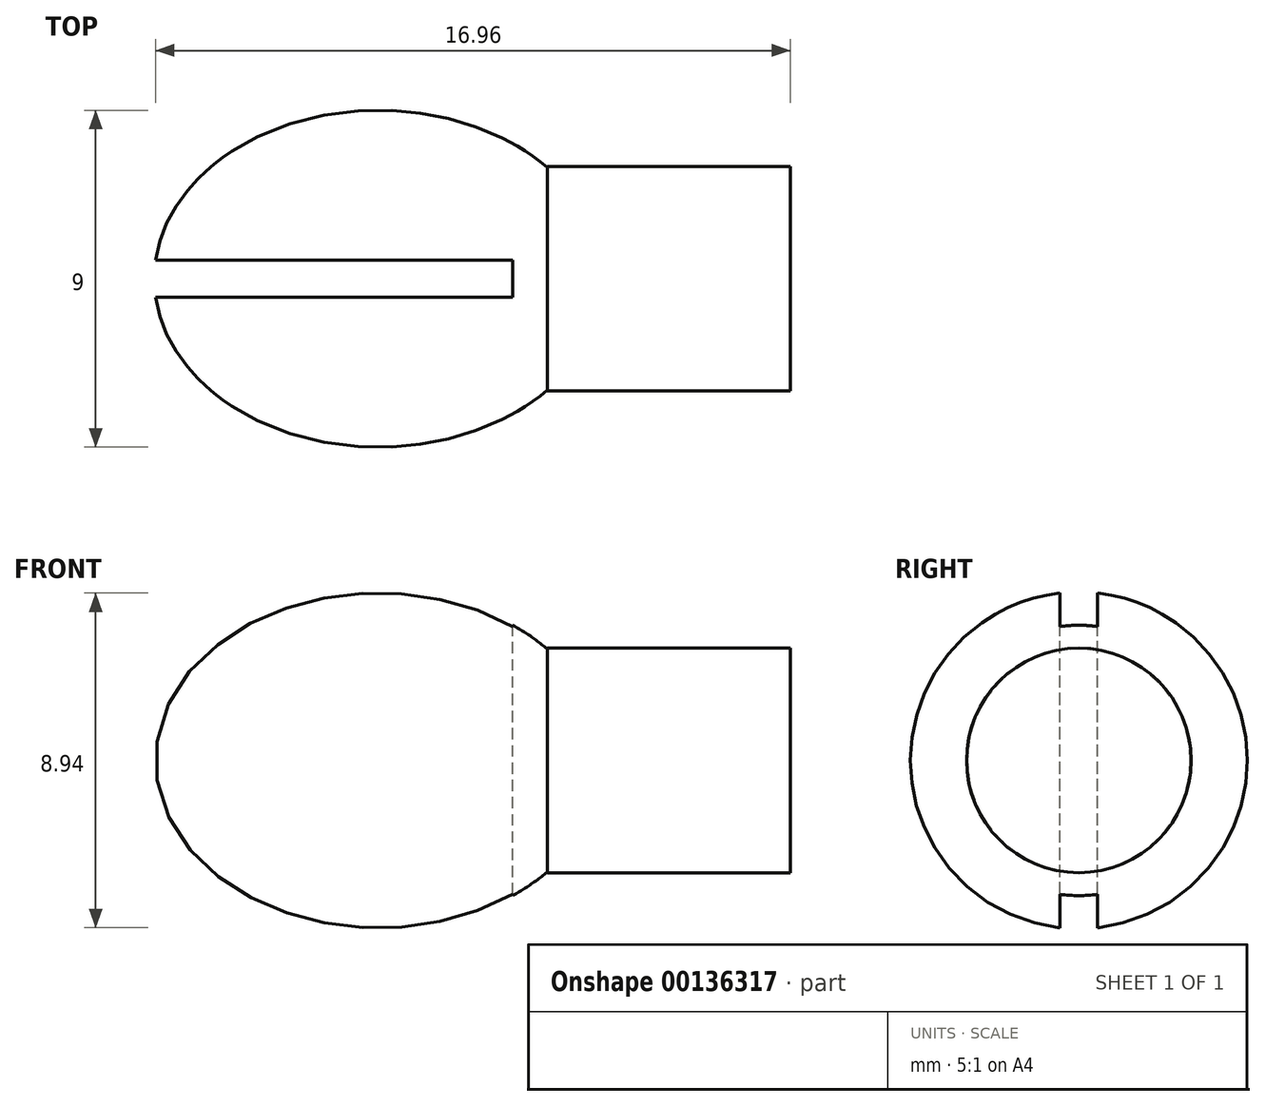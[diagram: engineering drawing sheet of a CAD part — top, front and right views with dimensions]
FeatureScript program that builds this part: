
annotation { "Feature Type Name" : "Feature", "Feature Type Description" : "" }
export const myFeature = defineFeature(function(context is Context, id is Id, definition is map)
    precondition{}
    {
        {
            var Q0;
            Q0=qCreatedBy(makeId("Front.planeOp"),FACE);
            var sketch = newSketch(context, id + "F0", { "sketchPlane" : qUnion([Q0])});
            skEllipse(sketch, "E0", {"center": v(0, 0) * mm, "majorRadius": 6 * mm, "minorRadius": 4.5 * mm, "majorAxis": v(1, 0)});
            skLineSegment(sketch, "E1", {"start": v(-6, 0) * mm, "end": v(6, 0) * mm});
            skSolve(sketch);
        }
        {
            var Q0;
            {var subQ0=sQuery(id+"F0.wireOp",EDGE,"E1");Q0=makeQuery(id+"F0.imprint","IMPRINT",FACE,{"disambiguationData":[TD([[makeQuery(id+"F0.imprint","IMPRINT",EDGE,{"derivedFrom":subQ0}),1.0]])]});}
            var Q1;
            Q1=sQuery(id+"F0.wireOp",EDGE,"E1");
            revolve(context, id + "F1", {"entities" : qUnion([Q0]), "axis" : qUnion([Q1]), "revolveType" : RevolveType.FULL});
        }
        {
            var Q0;
            Q0=qCreatedBy(makeId("Front.planeOp"),FACE);
            var sketch = newSketch(context, id + "F2", { "sketchPlane" : qUnion([Q0])});
            skLineSegment(sketch, "E2", {"start": v(4.5, 3) * mm, "end": v(4.5, -3) * mm});
            skLineSegment(sketch, "E3", {"start": v(4.5, 3) * mm, "end": v(4.5, 3.6) * mm});
            skLineSegment(sketch, "E4", {"start": v(4.5, 3.6) * mm, "end": v(6.38, 3.6) * mm});
            skLineSegment(sketch, "E5", {"start": v(6.38, 3.6) * mm, "end": v(6.38, -3.79) * mm});
            skLineSegment(sketch, "E6", {"start": v(6.38, -3.79) * mm, "end": v(4.5, -3.79) * mm});
            skLineSegment(sketch, "E7", {"start": v(4.5, -3.79) * mm, "end": v(4.5, -3) * mm});
            skSolve(sketch);
        }
        {
            var Q0;
            Q0=makeQuery(id+"F2.imprint","IMPRINT",FACE,{"disambiguationData":[TD([[makeQuery(id+"F2.imprint","IMPRINT",EDGE,{"derivedFrom":sQuery(id+"F2.wireOp",EDGE,"E2")}),1.0]])]});
            extrude(context, id + "F3", {"entities" : qUnion([Q0]), "operationType" : NewBodyOperationType.REMOVE, "endBound" : BoundingType.SYMMETRIC, "oppositeDirection" : true, "depth" : 25 * mm});
        }
        {
            var Q0;
            Q0=makeQuery(id+"F3.boolean.opBoolean","COPY",FACE,{"derivedFrom":makeQuery(id+"F3.opExtrude","SWEPT_FACE",FACE,{"disambiguationData":[OSD([sQuery(id+"F2.wireOp",EDGE,"E2"),sQuery(id+"F2.wireOp",EDGE,"E3")])]})});
            var sketch = newSketch(context, id + "F4", { "sketchPlane" : qUnion([Q0])});
            skCircle(sketch, "E8", {"center": v(0, 0) * mm, "radius": 3 * mm});
            skSolve(sketch);
        }
        {
            var Q0;
            Q0 = qSketchRegion(id + "F4", true);
            extrude(context, id + "F5", {"entities" : qUnion([Q0]), "operationType" : NewBodyOperationType.ADD, "depth" : 6.5 * mm});
        }
        {
            var Q0;
            Q0=qCreatedBy(makeId("Top.planeOp"),FACE);
            var sketch = newSketch(context, id + "F6", { "sketchPlane" : qUnion([Q0])});
            skLineSegment(sketch, "E9.bottom", {"start": v(3.58, -0.5) * mm, "end": v(-15.42, -0.5) * mm});
            skLineSegment(sketch, "E9.top", {"start": v(3.58, 0.5) * mm, "end": v(-15.42, 0.5) * mm});
            skLineSegment(sketch, "E9.left", {"start": v(3.58, -0.5) * mm, "end": v(3.58, 0.5) * mm});
            skLineSegment(sketch, "E9.right", {"start": v(-15.42, -0.5) * mm, "end": v(-15.42, 0.5) * mm});
            skPoint(sketch, "E9.middle", {"position": v(-5.92, 0) * mm});
            skSolve(sketch);
        }
        {
            var Q0;
            Q0=makeQuery(id+"F6.imprint","IMPRINT",FACE,{"disambiguationData":[TD([[makeQuery(id+"F6.imprint","IMPRINT",EDGE,{"derivedFrom":sQuery(id+"F6.wireOp",EDGE,"E9.bottom")}),-1.0]])]});
            extrude(context, id + "F7", {"entities" : qUnion([Q0]), "operationType" : NewBodyOperationType.REMOVE, "endBound" : BoundingType.SYMMETRIC, "oppositeDirection" : true, "depth" : 25 * mm});
        }
    });
